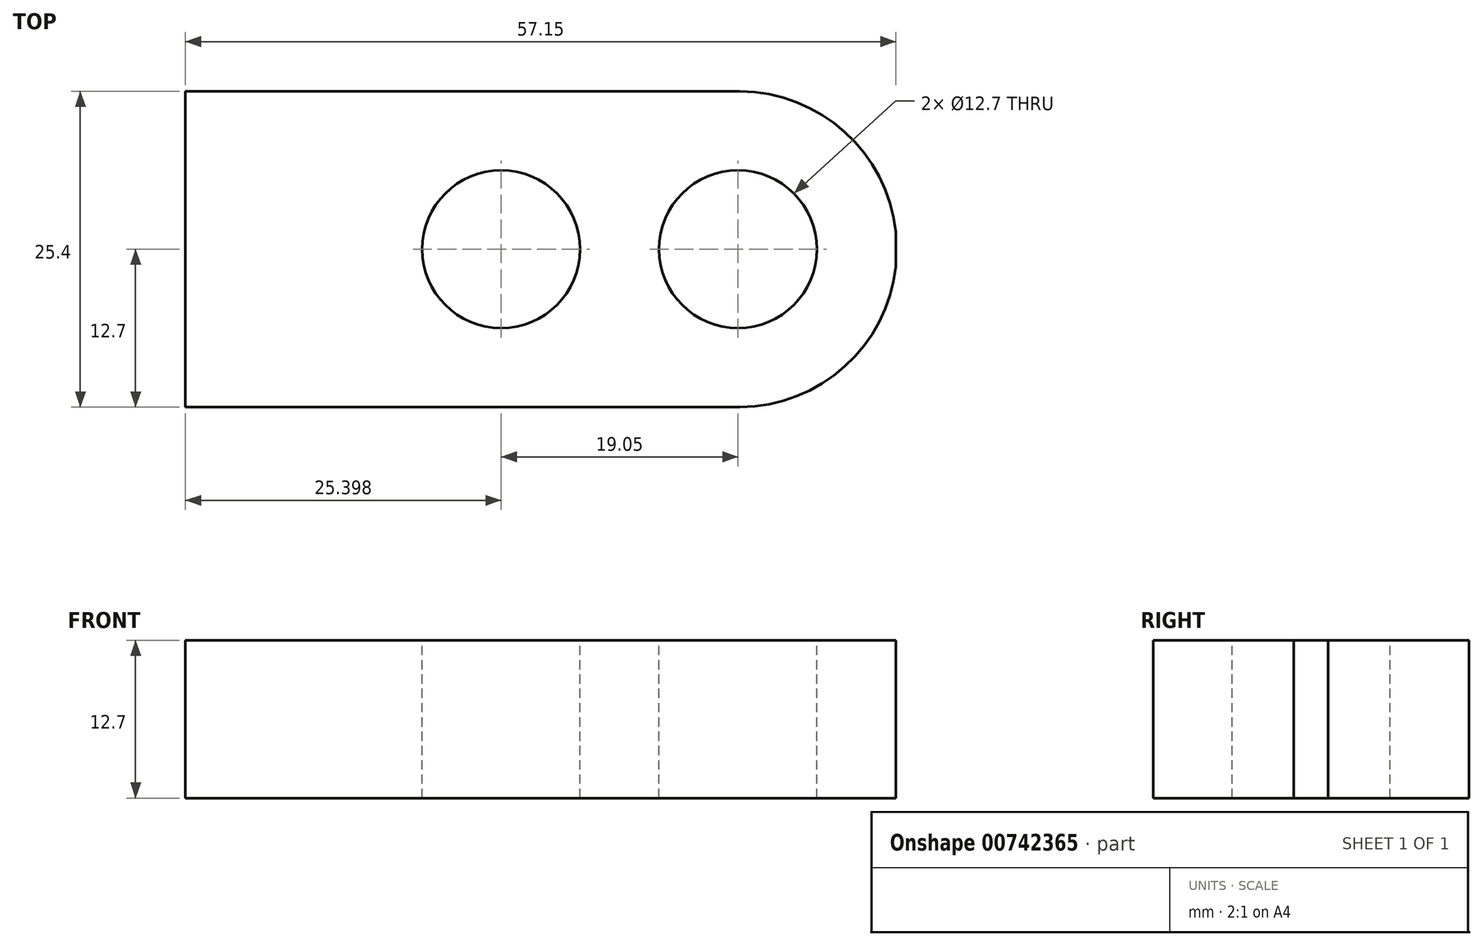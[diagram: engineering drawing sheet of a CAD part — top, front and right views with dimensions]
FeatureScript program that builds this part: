
annotation { "Feature Type Name" : "Feature", "Feature Type Description" : "" }
export const myFeature = defineFeature(function(context is Context, id is Id, definition is map)
    precondition{}
    {
        {
            var Q0;
            Q0=qCreatedBy(makeId("Front.planeOp"),FACE);
            var sketch = newSketch(context, id + "F0", { "sketchPlane" : qUnion([Q0])});
            skLineSegment(sketch, "E0", {"start": v(-23.84, 0) * mm, "end": v(33.3, 0) * mm});
            skLineSegment(sketch, "E1", {"start": v(33.3, 0) * mm, "end": v(33.3, 12.7) * mm});
            skLineSegment(sketch, "E2", {"start": v(33.3, 12.7) * mm, "end": v(-11.14, 12.7) * mm});
            skLineSegment(sketch, "E3", {"start": v(-11.14, 12.7) * mm, "end": v(-11.14, 44.45) * mm});
            skLineSegment(sketch, "E4", {"start": v(-11.14, 44.45) * mm, "end": v(-23.84, 44.45) * mm});
            skLineSegment(sketch, "E5", {"start": v(-23.84, 44.45) * mm, "end": v(-23.84, 0) * mm});
            skSolve(sketch);
        }
        {
            var Q0;
            Q0=makeQuery(id+"F0.imprint","IMPRINT",FACE,{"disambiguationData":[TD([[makeQuery(id+"F0.imprint","IMPRINT",EDGE,{"derivedFrom":sQuery(id+"F0.wireOp",EDGE,"E0")}),1.0]])]});
            extrude(context, id + "F1", {"entities" : qUnion([Q0]), "depth" : 25.4 * mm, "offsetDistance" : 25.4 * mm});
        }
        {
            var Q0;
            Q0=makeQuery(id+"F1.opExtrude","SWEPT_FACE",FACE,{"disambiguationData":[OSD([sQuery(id+"F0.wireOp",EDGE,"E2")])]});
            var sketch = newSketch(context, id + "F2", { "sketchPlane" : qUnion([Q0])});
            skCircle(sketch, "E6", {"center": v(20.6, -12.7) * mm, "radius": 6.35 * mm});
            skCircle(sketch, "E7", {"center": v(1.56, -12.7) * mm, "radius": 6.35 * mm});
            skArc(sketch, "E8", {"start": v(20.6, -25.4) * mm, "mid": v(33.38, -12.7) * mm, "end": v(20.6, 0) * mm});
            skSolve(sketch);
        }
        {
            var Q0;
            Q0=makeQuery(id+"F2.imprint","IMPRINT",FACE,{"disambiguationData":[TD([[makeQuery(id+"F2.imprint","IMPRINT",EDGE,{"derivedFrom":sQuery(id+"F2.wireOp",EDGE,"E7")}),1.0]])]});
            var Q1;
            Q1=makeQuery(id+"F2.imprint","IMPRINT",FACE,{"disambiguationData":[TD([[makeQuery(id+"F2.imprint","IMPRINT",EDGE,{"derivedFrom":sQuery(id+"F2.wireOp",EDGE,"E6")}),1.0]])]});
            var Q2;
            {var subQ0=sQuery(id+"F2.wireOp",EDGE,"E8");var subQ1=sQuery(id+"F0.wireOp",EDGE,"E2");var subQ2=makeQuery(id+"F1.opExtrude","CAP_EDGE",EDGE,{"disambiguationData":[OSD([subQ1])],"isStart":false});var subQ3=makeQuery(id+"F2.imprint","INTERSECT",VERTEX,{"disambiguationData":[OD(1.0)],"derivedFrom":[subQ2,subQ0]});Q2=makeQuery(id+"F2.imprint","IMPRINT",FACE,{"disambiguationData":[TD([[makeQuery(id+"F2.imprint","IMPRINT",EDGE,{"disambiguationData":[TD([[subQ3,-1.0]])],"derivedFrom":subQ0}),-1.0]])]});}
            var Q3;
            {var subQ0=sQuery(id+"F2.wireOp",EDGE,"E8");var subQ1=sQuery(id+"F0.wireOp",EDGE,"E2");var subQ4=makeQuery(id+"F1.opExtrude","CAP_EDGE",EDGE,{"disambiguationData":[OSD([subQ1])],"isStart":true});var subQ5=makeQuery(id+"F2.imprint","INTERSECT",VERTEX,{"disambiguationData":[OD(1.0)],"derivedFrom":[subQ4,subQ0]});Q3=makeQuery(id+"F2.imprint","IMPRINT",FACE,{"disambiguationData":[TD([[makeQuery(id+"F2.imprint","IMPRINT",EDGE,{"disambiguationData":[TD([[subQ5,1.0]])],"derivedFrom":subQ0}),-1.0]])]});}
            extrude(context, id + "F3", {"entities" : qUnion([Q0, Q1, Q2, Q3]), "operationType" : NewBodyOperationType.REMOVE, "endBound" : BoundingType.THROUGH_ALL, "oppositeDirection" : true, "depth" : 25.4 * mm, "offsetDistance" : 25.4 * mm});
        }
        {
            var Q0;
            Q0=makeQuery(id+"F1.opExtrude","SWEPT_FACE",FACE,{"disambiguationData":[OSD([sQuery(id+"F0.wireOp",EDGE,"E3")])]});
            var sketch = newSketch(context, id + "F4", { "sketchPlane" : qUnion([Q0])});
            skCircle(sketch, "E9", {"center": v(-12.7, 31.75) * mm, "radius": 6.35 * mm});
            skLineSegment(sketch, "E10", {"start": v(-6.38, 31.17) * mm, "end": v(-6.38, 44.45) * mm});
            skLineSegment(sketch, "E11", {"start": v(-19.05, 31.54) * mm, "end": v(-19.05, 44.45) * mm});
            skArc(sketch, "E12", {"start": v(0, 31.54) * mm, "mid": v(-12.7, 44.39) * mm, "end": v(-25.4, 31.54) * mm});
            skSolve(sketch);
        }
        {
            var Q0;
            {var subQ0=sQuery(id+"F4.wireOp",EDGE,"E11");var subQ1=sQuery(id+"F4.wireOp",EDGE,"E9");var subQ2=makeQuery(id+"F4.imprint","INTERSECT",VERTEX,{"disambiguationData":[OD(1.0)],"derivedFrom":[subQ1,subQ0]});Q0=makeQuery(id+"F4.imprint","IMPRINT",FACE,{"disambiguationData":[TD([[makeQuery(id+"F4.imprint","IMPRINT",EDGE,{"disambiguationData":[TD([[subQ2,1.0]])],"derivedFrom":subQ1}),1.0]])]});}
            var Q1;
            {var subQ0=sQuery(id+"F4.wireOp",EDGE,"E11");var subQ1=sQuery(id+"F4.wireOp",EDGE,"E9");var subQ2=makeQuery(id+"F4.imprint","INTERSECT",VERTEX,{"disambiguationData":[OD(1.0)],"derivedFrom":[subQ1,subQ0]});Q1=makeQuery(id+"F4.imprint","IMPRINT",FACE,{"disambiguationData":[TD([[makeQuery(id+"F4.imprint","IMPRINT",EDGE,{"disambiguationData":[TD([[subQ2,1.0]])],"derivedFrom":subQ1}),-1.0]])]});}
            var Q2;
            {var subQ0=sQuery(id+"F4.wireOp",EDGE,"E11");var subQ4=sQuery(id+"F4.wireOp",EDGE,"E12");var subQ5=makeQuery(id+"F4.imprint","INTERSECT",VERTEX,{"derivedFrom":[subQ0,subQ4]});Q2=makeQuery(id+"F4.imprint","IMPRINT",FACE,{"disambiguationData":[TD([[makeQuery(id+"F4.imprint","IMPRINT",EDGE,{"disambiguationData":[TD([[subQ5,-1.0]])],"derivedFrom":subQ4}),-1.0]])]});}
            var Q3;
            {var subQ0=sQuery(id+"F4.wireOp",EDGE,"E10");var subQ4=sQuery(id+"F4.wireOp",EDGE,"E12");var subQ5=makeQuery(id+"F4.imprint","INTERSECT",VERTEX,{"derivedFrom":[subQ0,subQ4]});Q3=makeQuery(id+"F4.imprint","IMPRINT",FACE,{"disambiguationData":[TD([[makeQuery(id+"F4.imprint","IMPRINT",EDGE,{"disambiguationData":[TD([[subQ5,1.0]])],"derivedFrom":subQ4}),-1.0]])]});}
            extrude(context, id + "F5", {"entities" : qUnion([Q0, Q1, Q2, Q3]), "operationType" : NewBodyOperationType.REMOVE, "endBound" : BoundingType.THROUGH_ALL, "oppositeDirection" : true, "depth" : 25.4 * mm, "offsetDistance" : 25.4 * mm});
        }
        {
            var Q0;
            {var subQ0=sQuery(id+"F0.wireOp",EDGE,"E4");var subQ2=sQuery(id+"F0.wireOp",EDGE,"E3");Q0=makeQuery(id+"F5.boolean.opBoolean","SPLIT",FACE,{"disambiguationData":[TD([makeQuery(id+"F1.opExtrude","SWEPT_FACE",FACE,{"disambiguationData":[OSD([subQ0])]})])],"derivedFrom":makeQuery(id+"F1.opExtrude","SWEPT_FACE",FACE,{"disambiguationData":[OSD([subQ2])]})});}
            extrude(context, id + "F6", {"entities" : qUnion([Q0]), "operationType" : NewBodyOperationType.REMOVE, "endBound" : BoundingType.THROUGH_ALL, "oppositeDirection" : true, "depth" : 25.4 * mm, "offsetDistance" : 25.4 * mm});
        }
    });
